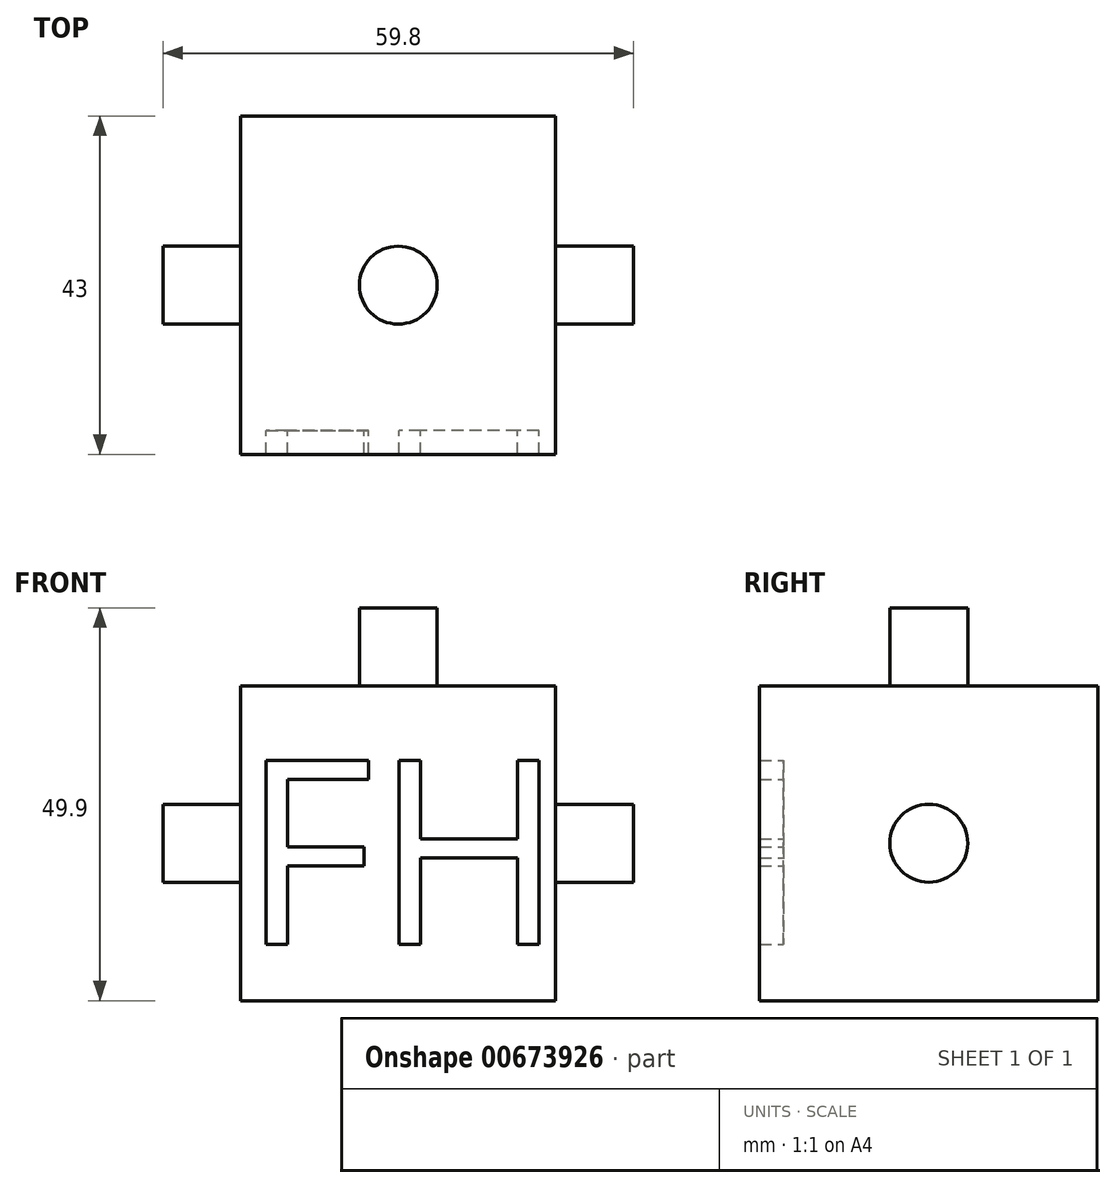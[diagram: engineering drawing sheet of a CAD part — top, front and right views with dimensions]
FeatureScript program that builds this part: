
annotation { "Feature Type Name" : "Feature", "Feature Type Description" : "" }
export const myFeature = defineFeature(function(context is Context, id is Id, definition is map)
    precondition{}
    {
        {
            var Q0;
            Q0=qCreatedBy(makeId("Front.planeOp"),FACE);
            var sketch = newSketch(context, id + "F0", { "sketchPlane" : qUnion([Q0])});
            skLineSegment(sketch, "E0.bottom", {"start": v(0, 0) * mm, "end": v(-40, 0) * mm});
            skLineSegment(sketch, "E0.top", {"start": v(0, 40) * mm, "end": v(-40, 40) * mm});
            skLineSegment(sketch, "E0.left", {"start": v(0, 0) * mm, "end": v(0, 40) * mm});
            skLineSegment(sketch, "E0.right", {"start": v(-40, 0) * mm, "end": v(-40, 40) * mm});
            skSolve(sketch);
        }
        {
            var Q0;
            Q0=makeQuery(id+"F0.imprint","IMPRINT",FACE,{"disambiguationData":[TD([[makeQuery(id+"F0.imprint","IMPRINT",EDGE,{"derivedFrom":sQuery(id+"F0.wireOp",EDGE,"E0.bottom")}),-1.0]])]});
            extrude(context, id + "F1", {"entities" : qUnion([Q0]), "depth" : 40 * mm, "offsetDistance" : 25 * mm});
        }
        {
            var Q0;
            Q0=makeQuery(id+"F1.opExtrude","CAP_FACE",FACE,{"disambiguationData":[OSD([sQuery(id+"F0.wireOp",EDGE,"E0.bottom"),sQuery(id+"F0.wireOp",EDGE,"E0.top"),sQuery(id+"F0.wireOp",EDGE,"E0.left"),sQuery(id+"F0.wireOp",EDGE,"E0.right")])],"isStart":false});
            var sketch = newSketch(context, id + "F2", { "sketchPlane" : qUnion([Q0])});
            skText(sketch, "E1", { "text": "FH", "fontName": "OpenSans-Regular.ttf"});
            const initialGuessF2  = {"E1": [-0.04, 0.00712, 1, 0, 0.02359]};
            skSetInitialGuess(sketch, initialGuessF2);
            skSolve(sketch);
        }
        {
            var Q0;
            Q0=makeQuery(id+"F2.imprint","IMPRINT",FACE,{"disambiguationData":[TD([[makeQuery(id+"F2.imprint","IMPRINT",EDGE,{"derivedFrom":sQuery(id+"F2.wireOp",EDGE,"E1.sketch_text.stroke-0")}),1.0]])]});
            extrude(context, id + "F3", {"entities" : qUnion([Q0]), "operationType" : NewBodyOperationType.ADD, "depth" : 3 * mm, "offsetDistance" : 25 * mm});
        }
        {
            var Q0;
            {var subQ0=sQuery(id+"F0.wireOp",EDGE,"E0.top");Q0=makeQuery(id+"F3.boolean.opBoolean","MERGE",FACE,{"derivedFrom":[makeQuery(id+"F1.opExtrude","SWEPT_FACE",FACE,{"disambiguationData":[OSD([subQ0])]}),makeQuery(id+"F3.opExtrude","SWEPT_FACE",FACE,{"disambiguationData":[OSD([subQ0])]})]});}
            var sketch = newSketch(context, id + "F4", { "sketchPlane" : qUnion([Q0])});
            skCircle(sketch, "E2", {"center": v(-20, -21.5) * mm, "radius": 4.95 * mm});
            skPoint(sketch, "E2.centerSnap0", {"position": v(0, -21.5) * mm});
            skPoint(sketch, "E2.centerSnap1", {"position": v(-20, -43) * mm});
            skSolve(sketch);
        }
        {
            var Q0;
            Q0=makeQuery(id+"F4.imprint","IMPRINT",FACE,{"disambiguationData":[TD([[makeQuery(id+"F4.imprint","IMPRINT",EDGE,{"derivedFrom":sQuery(id+"F4.wireOp",EDGE,"E2")}),1.0]])]});
            extrude(context, id + "F5", {"entities" : qUnion([Q0]), "operationType" : NewBodyOperationType.ADD, "depth" : 9.9 * mm, "offsetDistance" : 25 * mm});
        }
        {
            var Q0;
            {var subQ0=sQuery(id+"F0.wireOp",EDGE,"E0.right");Q0=makeQuery(id+"F3.boolean.opBoolean","MERGE",FACE,{"derivedFrom":[makeQuery(id+"F1.opExtrude","SWEPT_FACE",FACE,{"disambiguationData":[OSD([subQ0])]}),makeQuery(id+"F3.opExtrude","SWEPT_FACE",FACE,{"disambiguationData":[OSD([subQ0])]})]});}
            var sketch = newSketch(context, id + "F6", { "sketchPlane" : qUnion([Q0])});
            skCircle(sketch, "E3", {"center": v(21.5, 20) * mm, "radius": 4.95 * mm});
            skPoint(sketch, "E3.centerSnap0", {"position": v(43, 20) * mm});
            skPoint(sketch, "E3.centerSnap1", {"position": v(21.5, 0) * mm});
            skSolve(sketch);
        }
        {
            var Q0;
            Q0=makeQuery(id+"F6.imprint","IMPRINT",FACE,{"disambiguationData":[TD([[makeQuery(id+"F6.imprint","IMPRINT",EDGE,{"derivedFrom":sQuery(id+"F6.wireOp",EDGE,"E3")}),1.0]])]});
            extrude(context, id + "F7", {"entities" : qUnion([Q0]), "operationType" : NewBodyOperationType.ADD, "depth" : 9.9 * mm, "offsetDistance" : 25 * mm});
        }
        {
            var Q0;
            {var subQ0=sQuery(id+"F0.wireOp",EDGE,"E0.left");Q0=makeQuery(id+"F3.boolean.opBoolean","MERGE",FACE,{"derivedFrom":[makeQuery(id+"F1.opExtrude","SWEPT_FACE",FACE,{"disambiguationData":[OSD([subQ0])]}),makeQuery(id+"F3.opExtrude","SWEPT_FACE",FACE,{"disambiguationData":[OSD([subQ0])]})]});}
            var sketch = newSketch(context, id + "F8", { "sketchPlane" : qUnion([Q0])});
            skCircle(sketch, "E4", {"center": v(-21.5, 20) * mm, "radius": 4.95 * mm});
            skPoint(sketch, "E4.centerSnap0", {"position": v(0, 20) * mm});
            skPoint(sketch, "E4.centerSnap1", {"position": v(-21.5, 0) * mm});
            skSolve(sketch);
        }
        {
            var Q0;
            Q0=makeQuery(id+"F8.imprint","IMPRINT",FACE,{"disambiguationData":[TD([[makeQuery(id+"F8.imprint","IMPRINT",EDGE,{"derivedFrom":sQuery(id+"F8.wireOp",EDGE,"E4")}),1.0]])]});
            extrude(context, id + "F9", {"entities" : qUnion([Q0]), "operationType" : NewBodyOperationType.ADD, "depth" : 9.9 * mm, "offsetDistance" : 25 * mm});
        }
    });
